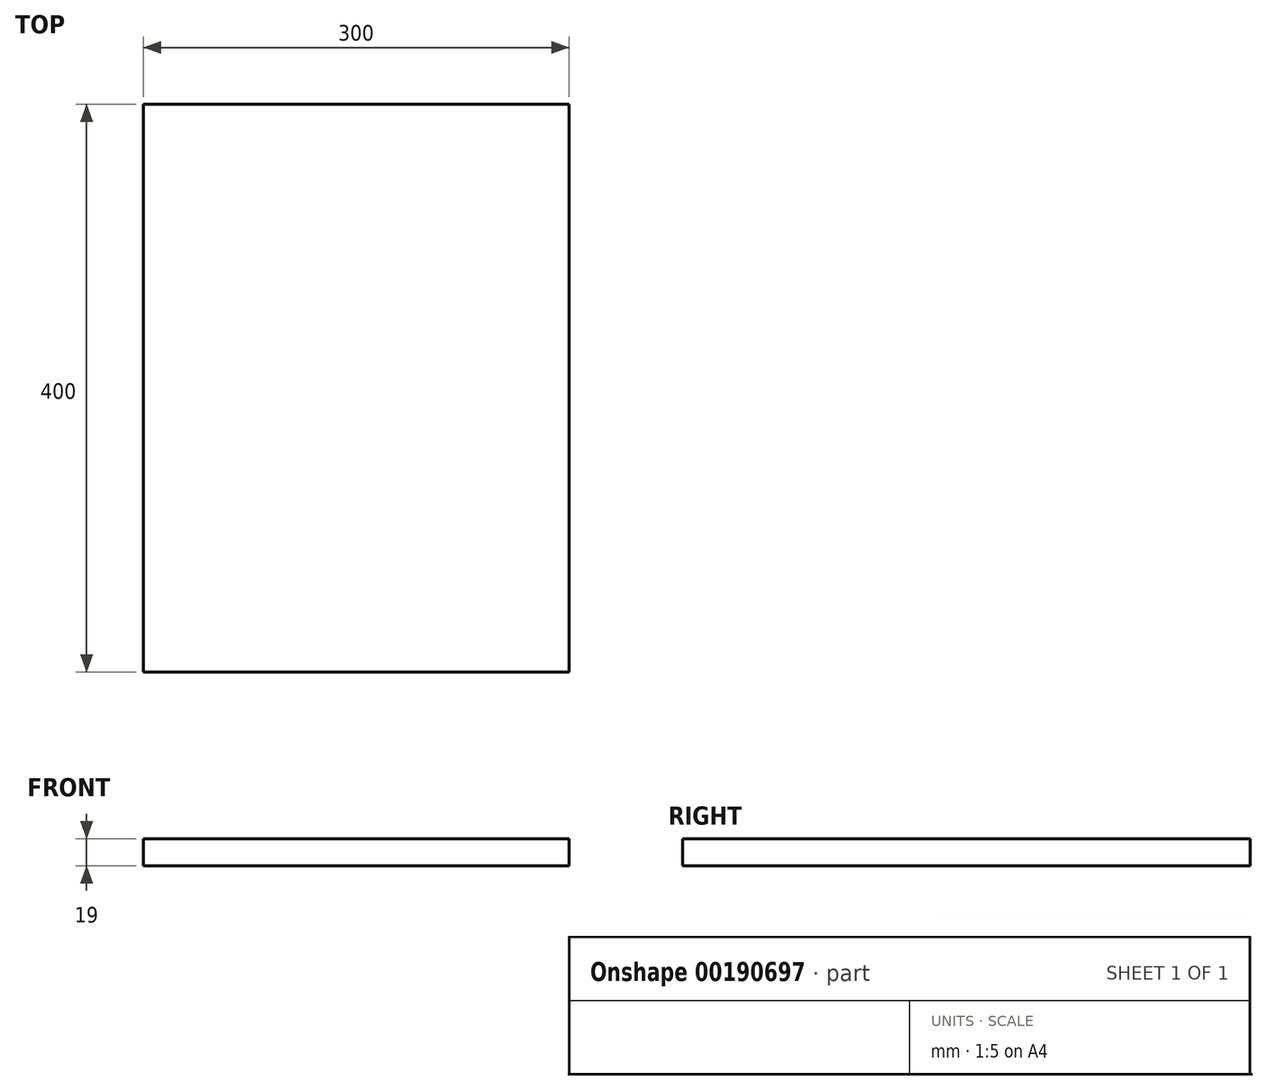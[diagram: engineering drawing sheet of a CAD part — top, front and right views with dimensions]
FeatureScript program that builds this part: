
annotation { "Feature Type Name" : "Feature", "Feature Type Description" : "" }
export const myFeature = defineFeature(function(context is Context, id is Id, definition is map)
    precondition{}
    {
        {
            var Q0;
            Q0=qCreatedBy(makeId("Top.planeOp"),FACE);
            var sketch = newSketch(context, id + "F0", { "sketchPlane" : qUnion([Q0])});
            skLineSegment(sketch, "E0.bottom", {"start": v(-127.86, -208.19) * mm, "end": v(172.14, -208.19) * mm});
            skLineSegment(sketch, "E0.top", {"start": v(-127.86, 191.81) * mm, "end": v(172.14, 191.81) * mm});
            skLineSegment(sketch, "E0.left", {"start": v(-127.86, -208.19) * mm, "end": v(-127.86, 191.81) * mm});
            skLineSegment(sketch, "E0.right", {"start": v(172.14, -208.19) * mm, "end": v(172.14, 191.81) * mm});
            skSolve(sketch);
        }
        {
            var Q0;
            Q0 = qSketchRegion(id + "F0", true);
            extrude(context, id + "F1", {"entities" : qUnion([Q0]), "depth" : 19 * mm});
        }
    });
